# Revit family: Power-ModularDevices-GEWISS-90AM-SPD_TYPE2_DC
name_source: partatom
category: Apparecchi elettrici
revit_build: Autodesk Revit 2016 (Build: 20161004_0715(x64)
units: mm (PartAtom-declared; Revit-internal decimal feet)

## family parameters
Condiviso = No
Host = Superficie
Mantenere orientamento annotazione = Sì
Numero OmniClass = 23.80.50.00
Punto di calcolo locali = Sì
Quota connettore circolare = Usa diametro
Taglio con vuoti quando caricato = No
Tipo di parte = Normale
Titolo OmniClass = Terminals for Power Supply

## types (2) — shared parameters
Catalogue = POWER
Catalogue Range = 90 AM
Electrocod = 0642
IDF = 3aaded6a-a6ee-4751-8fd7-1d519c232e27
IDT = dce585a3-ae1f-4300-811f-7f20ca7b728c
Immagine tipo = GWD6426.jpg
Maximum discharge current: = 40KA
No. Chorus modules = 3
No. of modules EN 50022 = 3
Numero di poli = 1
Produttore = GEWISS S.p.A.
Prospetto di default = 1219 mm
SEO = Limiter
Spostamento_x = -340 mm
Technical sheet = https://www.gewiss.com
Type = 2 - For photovoltaic applications
Type: = 2 - For photovoltaic applications
URL = https://www.gewiss.com
Version file RFA = 18.0
carico = Altro
potenza in watt = 1000 V

## per-type parameters (varying)
| type | Descrizione | EAN code | Modello | Rated voltage | Rated voltage DC |
| GWD6428 - LST - SPD 3P 40KA 1000V DC T2 | LST - SPD 3P 40KA 1000V DC T2 | 8011564775046 | GWD6428 | 1000Vdc | 1000V |
| GWD6426 - LST - SPD 3P 40KA 600V DC T2 | LST - SPD 3P 40KA 600V DC T2 | 8011564775039 | GWD6426 | 600Vdc | 600V |
